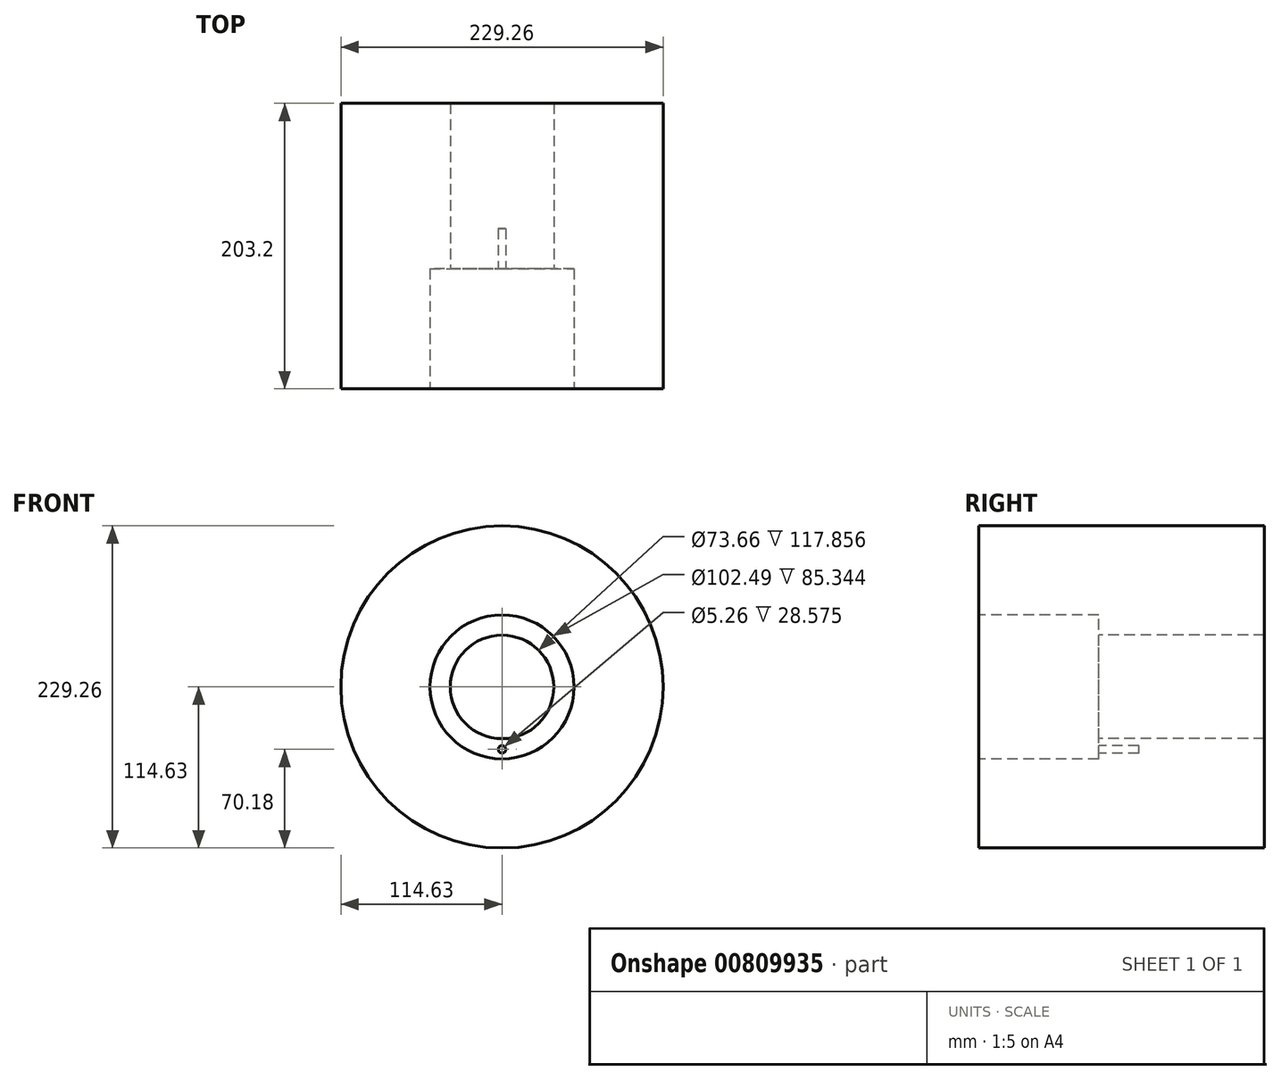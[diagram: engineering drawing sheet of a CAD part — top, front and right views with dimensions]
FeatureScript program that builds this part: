
annotation { "Feature Type Name" : "Feature", "Feature Type Description" : "" }
export const myFeature = defineFeature(function(context is Context, id is Id, definition is map)
    precondition{}
    {
        {
            var Q0;
            Q0=qCreatedBy(makeId("Front.planeOp"),FACE);
            var sketch = newSketch(context, id + "F0", { "sketchPlane" : qUnion([Q0])});
            skCircle(sketch, "E0", {"center": v(0, 0) * mm, "radius": 114.63 * mm});
            skSolve(sketch);
        }
        {
            var Q0;
            Q0 = qSketchRegion(id + "F0", true);
            extrude(context, id + "F1", {"entities" : qUnion([Q0]), "depth" : 203.2 * mm, "offsetDistance" : 25.4 * mm});
        }
        {
            var Q0;
            Q0=makeQuery(id+"F1.opExtrude","CAP_FACE",FACE,{"disambiguationData":[OSD([sQuery(id+"F0.wireOp",EDGE,"E0")])],"isStart":false});
            var sketch = newSketch(context, id + "F2", { "sketchPlane" : qUnion([Q0])});
            skCircle(sketch, "E1", {"center": v(0, 0) * mm, "radius": 36.83 * mm});
            skSolve(sketch);
        }
        {
            var Q0;
            Q0 = qSketchRegion(id + "F2", true);
            extrude(context, id + "F3", {"entities" : qUnion([Q0]), "operationType" : NewBodyOperationType.REMOVE, "oppositeDirection" : true, "depth" : 355.6 * mm, "offsetDistance" : 25.4 * mm});
        }
        {
            var Q0;
            Q0=makeQuery(id+"F1.opExtrude","CAP_FACE",FACE,{"disambiguationData":[OSD([sQuery(id+"F0.wireOp",EDGE,"E0")])],"isStart":false});
            var sketch = newSketch(context, id + "F4", { "sketchPlane" : qUnion([Q0])});
            skCircle(sketch, "E2", {"center": v(0, 0) * mm, "radius": 51.24 * mm});
            skSolve(sketch);
        }
        {
            var Q0;
            Q0 = qSketchRegion(id + "F4", true);
            extrude(context, id + "F5", {"entities" : qUnion([Q0]), "operationType" : NewBodyOperationType.REMOVE, "oppositeDirection" : true, "depth" : 85.34 * mm, "offsetDistance" : 25.4 * mm});
        }
        {
            var Q0;
            Q0=makeQuery(id+"F5.boolean.opBoolean","COPY",FACE,{"derivedFrom":makeQuery(id+"F5.opExtrude","CAP_FACE",FACE,{"disambiguationData":[OSD([sQuery(id+"F4.wireOp",EDGE,"E2")])],"isStart":false})});
            var sketch = newSketch(context, id + "F6", { "sketchPlane" : qUnion([Q0])});
            skCircle(sketch, "E3", {"center": v(0, -44.45) * mm, "radius": 2.63 * mm});
            skSolve(sketch);
        }
        {
            var Q0;
            Q0 = qSketchRegion(id + "F6", true);
            extrude(context, id + "F7", {"entities" : qUnion([Q0]), "operationType" : NewBodyOperationType.REMOVE, "oppositeDirection" : true, "depth" : 28.57 * mm, "offsetDistance" : 25.4 * mm});
        }
    });
